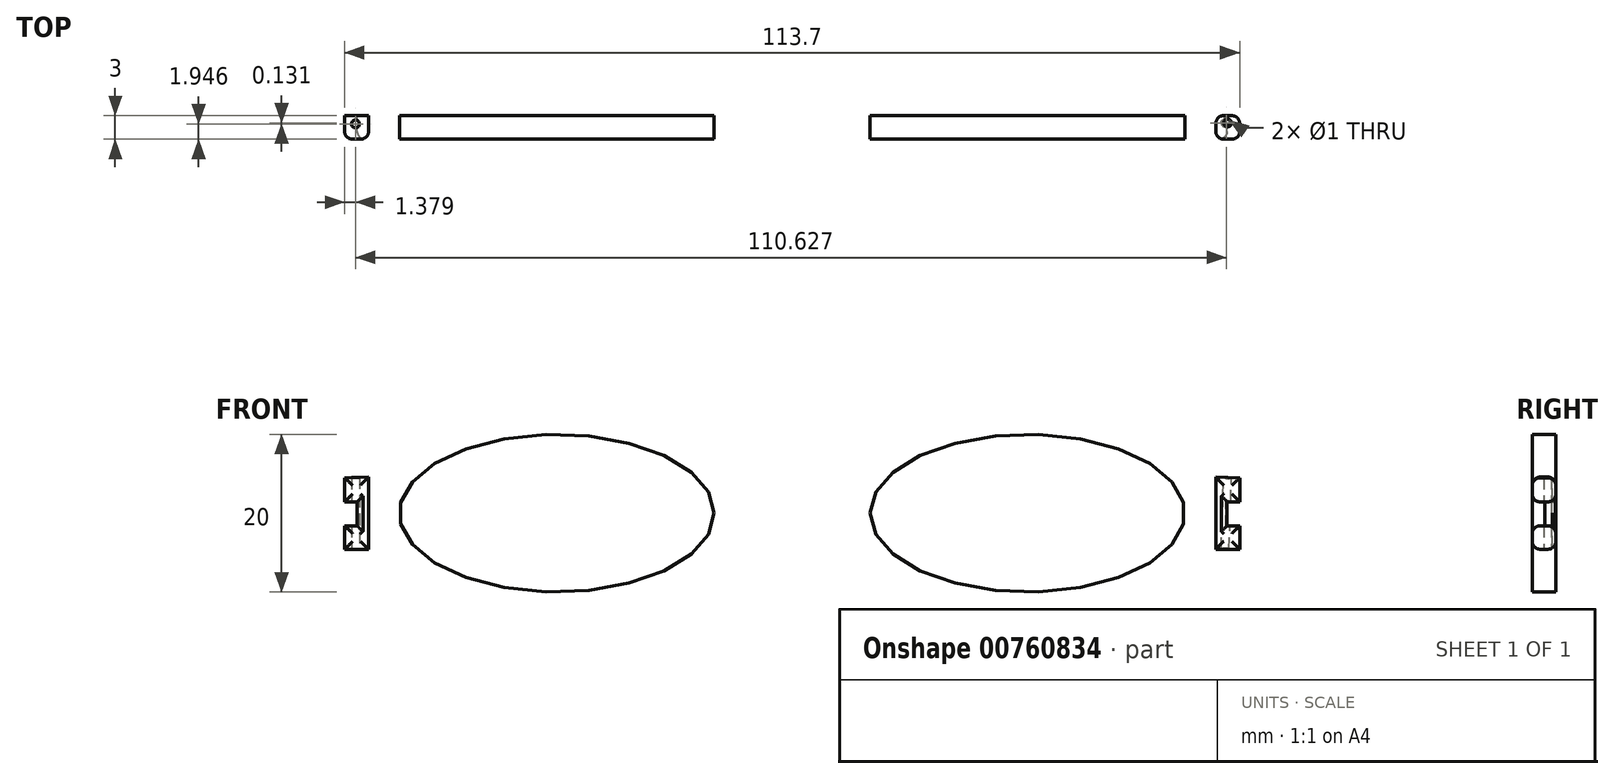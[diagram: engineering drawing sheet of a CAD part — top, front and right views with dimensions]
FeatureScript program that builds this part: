
annotation { "Feature Type Name" : "Feature", "Feature Type Description" : "" }
export const myFeature = defineFeature(function(context is Context, id is Id, definition is map)
    precondition{}
    {
        {
            var Q0;
            Q0=qCreatedBy(makeId("Front.planeOp"),FACE);
            var sketch = newSketch(context, id + "F0", { "sketchPlane" : qUnion([Q0])});
            skEllipse(sketch, "E0", {"center": v(-29.9, 0) * mm, "majorRadius": 20 * mm, "minorRadius": 10 * mm, "majorAxis": v(1, 0)});
            skFitSpline(sketch, "E1.0", {"points": [v(-5.03, -1.97) * mm, v(-4.83, 0) * mm, v(-5.03, 1.97) * mm, v(-5.6, 3.83) * mm, v(-6.45, 5.52) * mm, v(-7.54, 7.04) * mm, v(-8.82, 8.39) * mm, v(-10.74, 9.98) * mm, v(-13.45, 11.62) * mm, v(-16.52, 12.87) * mm, v(-19.17, 13.67) * mm, v(-21.91, 14.32) * mm, v(-24.76, 14.75) * mm, v(-27.68, 14.96) * mm, v(-29.9, 15.02) * mm, v(-32.12, 14.96) * mm, v(-35.04, 14.75) * mm, v(-37.89, 14.32) * mm, v(-40.63, 13.67) * mm, v(-43.28, 12.87) * mm, v(-46.35, 11.62) * mm, v(-49.06, 9.98) * mm, v(-50.98, 8.39) * mm, v(-52.26, 7.04) * mm, v(-53.35, 5.52) * mm, v(-54.2, 3.83) * mm, v(-54.77, 1.97) * mm, v(-54.97, 0) * mm, v(-54.77, -1.97) * mm, v(-54.2, -3.83) * mm, v(-53.35, -5.52) * mm, v(-52.26, -7.04) * mm, v(-50.98, -8.39) * mm, v(-49.06, -9.98) * mm, v(-46.35, -11.62) * mm, v(-43.28, -12.87) * mm, v(-40.63, -13.67) * mm, v(-37.89, -14.32) * mm, v(-35.04, -14.75) * mm, v(-32.12, -14.96) * mm, v(-29.9, -15.02) * mm, v(-27.68, -14.96) * mm, v(-24.76, -14.75) * mm, v(-21.91, -14.32) * mm, v(-19.17, -13.67) * mm, v(-16.52, -12.87) * mm, v(-13.45, -11.62) * mm, v(-10.74, -9.98) * mm, v(-8.82, -8.39) * mm, v(-7.54, -7.04) * mm, v(-6.45, -5.52) * mm, v(-5.6, -3.83) * mm, v(-5.03, -1.97) * mm, v(-4.83, 0) * mm, v(-5.03, 1.97) * mm, v(-5.03, -1.97) * mm]});
            skLineSegment(sketch, "E2", {"start": v(-53.81, 4.59) * mm, "end": v(-53.81, -4.59) * mm});
            skLineSegment(sketch, "E3", {"start": v(-53.81, -4.59) * mm, "end": v(-56.85, -4.59) * mm});
            skLineSegment(sketch, "E4", {"start": v(-56.85, -4.59) * mm, "end": v(-56.85, -1.6) * mm});
            skLineSegment(sketch, "E5", {"start": v(-56.85, -1.6) * mm, "end": v(-55.26, -1.6) * mm});
            skLineSegment(sketch, "E6", {"start": v(-55.26, -1.6) * mm, "end": v(-55.26, 1.44) * mm});
            skLineSegment(sketch, "E7", {"start": v(-55.26, 1.44) * mm, "end": v(-56.85, 1.44) * mm});
            skLineSegment(sketch, "E8", {"start": v(-56.85, 1.44) * mm, "end": v(-56.85, 4.48) * mm});
            skLineSegment(sketch, "E9", {"start": v(-56.85, 4.48) * mm, "end": v(-53.81, 4.59) * mm});
            skArc(sketch, "E10", {"start": v(5.1, 0) * mm, "mid": v(0.1, 5) * mm, "end": v(-4.9, 0) * mm});
            skArc(sketch, "E11.0", {"start": v(10.1, 0) * mm, "mid": v(0.1, 10) * mm, "end": v(-9.9, 0) * mm});
            skEllipse(sketch, "E12.MirrorC", {"center": v(29.9, 0) * mm, "majorRadius": 20 * mm, "minorRadius": 10 * mm, "majorAxis": v(-1, 0)});
            skLineSegment(sketch, "E13.MirrorCS", {"start": v(56.85, 4.48) * mm, "end": v(53.81, 4.59) * mm});
            skLineSegment(sketch, "E14.MirrorCS", {"start": v(56.85, 1.44) * mm, "end": v(56.85, 4.48) * mm});
            skLineSegment(sketch, "E15.MirrorCS", {"start": v(53.81, -4.59) * mm, "end": v(56.85, -4.59) * mm});
            skLineSegment(sketch, "E16.MirrorCS", {"start": v(56.85, -4.59) * mm, "end": v(56.85, -1.6) * mm});
            skLineSegment(sketch, "E17.MirrorCS", {"start": v(56.85, -1.6) * mm, "end": v(55.26, -1.6) * mm});
            skLineSegment(sketch, "E18.MirrorCS", {"start": v(55.26, -1.6) * mm, "end": v(55.26, 1.44) * mm});
            skLineSegment(sketch, "E19.MirrorCS", {"start": v(53.81, 4.59) * mm, "end": v(53.81, -4.59) * mm});
            skLineSegment(sketch, "E20.MirrorCS", {"start": v(55.26, 1.44) * mm, "end": v(56.85, 1.44) * mm});
            skFitSpline(sketch, "E21.0", {"points": [v(5.03, 1.97) * mm, v(4.83, 0) * mm, v(5.03, -1.97) * mm, v(5.6, -3.83) * mm, v(6.45, -5.52) * mm, v(7.54, -7.04) * mm, v(8.82, -8.39) * mm, v(10.74, -9.98) * mm, v(13.45, -11.62) * mm, v(16.52, -12.87) * mm, v(19.17, -13.67) * mm, v(21.91, -14.32) * mm, v(24.76, -14.75) * mm, v(27.68, -14.96) * mm, v(29.9, -15.02) * mm, v(32.12, -14.96) * mm, v(35.04, -14.75) * mm, v(37.89, -14.32) * mm, v(40.63, -13.67) * mm, v(43.28, -12.87) * mm, v(46.35, -11.62) * mm, v(49.06, -9.98) * mm, v(50.98, -8.39) * mm, v(52.26, -7.04) * mm, v(53.35, -5.52) * mm, v(54.2, -3.83) * mm, v(54.77, -1.97) * mm, v(54.97, 0) * mm, v(54.77, 1.97) * mm, v(54.2, 3.83) * mm, v(53.35, 5.52) * mm, v(52.26, 7.04) * mm, v(50.98, 8.39) * mm, v(49.06, 9.98) * mm, v(46.35, 11.62) * mm, v(43.28, 12.87) * mm, v(40.63, 13.67) * mm, v(37.89, 14.32) * mm, v(35.04, 14.75) * mm, v(32.12, 14.96) * mm, v(29.9, 15.02) * mm, v(27.68, 14.96) * mm, v(24.76, 14.75) * mm, v(21.91, 14.32) * mm, v(19.17, 13.67) * mm, v(16.52, 12.87) * mm, v(13.45, 11.62) * mm, v(10.74, 9.98) * mm, v(8.82, 8.39) * mm, v(7.54, 7.04) * mm, v(6.45, 5.52) * mm, v(5.6, 3.83) * mm, v(5.03, 1.97) * mm, v(4.83, 0) * mm, v(5.03, -1.97) * mm, v(5.03, 1.97) * mm]});
            skSolve(sketch);
        }
        {
            var Q0;
            Q0 = qSketchRegion(id + "F0", true);
            extrude(context, id + "F1", {"entities" : qUnion([Q0]), "depth" : 3 * mm, "offsetDistance" : 25 * mm});
        }
        {
            var Q0;
            Q0=makeQuery(id+"F1.opExtrude","CAP_FACE",FACE,{"disambiguationData":[OSD([sQuery(id+"F0.wireOp",EDGE,"E0"),sQuery(id+"F0.wireOp",EDGE,"E1.0"),sQuery(id+"F0.wireOp",EDGE,"E3"),sQuery(id+"F0.wireOp",EDGE,"E4"),sQuery(id+"F0.wireOp",EDGE,"E5"),sQuery(id+"F0.wireOp",EDGE,"E6"),sQuery(id+"F0.wireOp",EDGE,"E7"),sQuery(id+"F0.wireOp",EDGE,"E8"),sQuery(id+"F0.wireOp",EDGE,"E9"),sQuery(id+"F0.wireOp",EDGE,"E10"),sQuery(id+"F0.wireOp",EDGE,"E11.0"),sQuery(id+"F0.wireOp",EDGE,"E12.MirrorC"),sQuery(id+"F0.wireOp",EDGE,"E15.MirrorCS"),sQuery(id+"F0.wireOp",EDGE,"E16.MirrorCS"),sQuery(id+"F0.wireOp",EDGE,"E17.MirrorCS"),sQuery(id+"F0.wireOp",EDGE,"E18.MirrorCS"),sQuery(id+"F0.wireOp",EDGE,"E20.MirrorCS"),sQuery(id+"F0.wireOp",EDGE,"E13.MirrorCS"),sQuery(id+"F0.wireOp",EDGE,"E14.MirrorCS"),sQuery(id+"F0.wireOp",EDGE,"E21.0")])],"isStart":false});
            fillet(context, id + "F2", {"entities" : qUnion([Q0]), "radius" : 1 * mm, "tangentPropagation" : true, "allowEdgeOverflow" : false});
        }
        {
            var Q0;
            Q0=makeQuery(id+"F1.opExtrude","SWEPT_FACE",FACE,{"disambiguationData":[OSD([sQuery(id+"F0.wireOp",EDGE,"E13.MirrorCS")])]});
            var sketch = newSketch(context, id + "F3", { "sketchPlane" : qUnion([Q0])});
            skCircle(sketch, "E22", {"center": v(55.13, -0.92) * mm, "radius": 0.5 * mm});
            skSolve(sketch);
        }
        {
            var Q0;
            Q0 = qSketchRegion(id + "F3", true);
            extrude(context, id + "F4", {"entities" : qUnion([Q0]), "operationType" : NewBodyOperationType.REMOVE, "oppositeDirection" : true, "depth" : 50 * mm, "offsetDistance" : 25 * mm});
        }
        {
            var Q0;
            Q0=makeQuery(id+"F1.opExtrude","SWEPT_FACE",FACE,{"disambiguationData":[OSD([sQuery(id+"F0.wireOp",EDGE,"E3")])]});
            var sketch = newSketch(context, id + "F5", { "sketchPlane" : qUnion([Q0])});
            skCircle(sketch, "E23", {"center": v(-55.47, 1.05) * mm, "radius": 0.5 * mm});
            skSolve(sketch);
        }
        {
            var Q0;
            Q0=makeQuery(id+"F5.imprint","IMPRINT",FACE,{"disambiguationData":[TD([[makeQuery(id+"F5.imprint","IMPRINT",EDGE,{"derivedFrom":sQuery(id+"F5.wireOp",EDGE,"E23")}),1.0]])]});
            extrude(context, id + "F6", {"entities" : qUnion([Q0]), "operationType" : NewBodyOperationType.REMOVE, "oppositeDirection" : true, "depth" : 50 * mm, "offsetDistance" : 25 * mm});
        }
        {
            var Q0;
            Q0=makeQuery(id+"F1.opExtrude","CAP_FACE",FACE,{"disambiguationData":[OSD([sQuery(id+"F0.wireOp",EDGE,"E0"),sQuery(id+"F0.wireOp",EDGE,"E1.0"),sQuery(id+"F0.wireOp",EDGE,"E3"),sQuery(id+"F0.wireOp",EDGE,"E4"),sQuery(id+"F0.wireOp",EDGE,"E5"),sQuery(id+"F0.wireOp",EDGE,"E6"),sQuery(id+"F0.wireOp",EDGE,"E7"),sQuery(id+"F0.wireOp",EDGE,"E8"),sQuery(id+"F0.wireOp",EDGE,"E9"),sQuery(id+"F0.wireOp",EDGE,"E10"),sQuery(id+"F0.wireOp",EDGE,"E11.0"),sQuery(id+"F0.wireOp",EDGE,"E12.MirrorC"),sQuery(id+"F0.wireOp",EDGE,"E15.MirrorCS"),sQuery(id+"F0.wireOp",EDGE,"E16.MirrorCS"),sQuery(id+"F0.wireOp",EDGE,"E17.MirrorCS"),sQuery(id+"F0.wireOp",EDGE,"E18.MirrorCS"),sQuery(id+"F0.wireOp",EDGE,"E20.MirrorCS"),sQuery(id+"F0.wireOp",EDGE,"E13.MirrorCS"),sQuery(id+"F0.wireOp",EDGE,"E14.MirrorCS"),sQuery(id+"F0.wireOp",EDGE,"E21.0")])],"isStart":true});
            fillet(context, id + "F7", {"entities" : qUnion([Q0]), "radius" : 1 * mm, "tangentPropagation" : true, "allowEdgeOverflow" : false});
        }
    });
